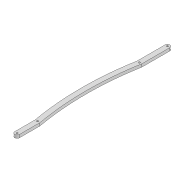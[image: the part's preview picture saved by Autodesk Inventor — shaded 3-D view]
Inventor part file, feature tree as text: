
AUTODESK INVENTOR PART (.ipt)
format: ipt  version: 2022 (Build 260153000, 153)  size: 106,496 bytes
history: native  units: mm
features: extrude x1, sketch x1
ambient origin geometry x8: Origin, YZ Plane, XZ Plane, XY Plane, X Axis, Y Axis, Z Axis, Center Point
bodies: Solid1 (feature_tree)
feature tree (2):
  extrude  "Extrusion1"  Depth=600.0mm
  sketch  "Sketch1"  dims[d0=3.3mm d1=3.3mm d2=10.0mm d3=312.648mm d6=6.0mm d7=0.0mm d10=3.3mm d11=42.6mm d12=3.3mm d13=254.274mm d16=600.0mm d17=600.0mm]
